# Revit family: Hager-IC-IP40-Transparent_Door-syst-NoHosted-PL-pl
name_source: partatom
category: Electrical Equipment
units: mm (PartAtom-declared; Revit-internal decimal feet)

## family parameters
Always vertical = Yes
Cut with Voids When Loaded = No
Panel Configuration = Two Columns, Circuits Across
Part Type = Panelboard
Room Calculation Point = No
Round Connector Dimension = Use Diameter
Shared = No
Work Plane-Based = Yes

## types (2) — shared parameters
Default Elevation = 1219 mm
EF000007 - Kolor = EV000202 - Biały
EF000116 - Numer RAL = 9010
EF000118 - Z płytą montażową = No
EF000266 - Liczba rzędów = 2
EF000339 - Rodzaj pokrywy = EV004216 - Drzwi
EF001062 - Wykonane zgodnie z Dyrektywą Kompatybilności Elektromagnetycznej EMC = No
EF001088 - Możliwość rozbudowy = Yes
EF001131 - Głębokość wewnętrzna = 72 mm  [stored 0.23622 ft]
EF001134 - Szyna DIN = Yes
EF001596 - Materiał obudowy = EV000139 - Tworzywo sztuczne
EF002950 - Szerokość wyrażona liczbą modułów = 12
EF004462 - Rodzaj zamknięcia = EV000154 - Inne
EF005474 - Stopień ochrony (IP) = EV006415 - IP40
EF006244 - Transparentna pokrywa/drzwi = Yes
EF006306 - Z zamkiem = No
EF009212 - Wykonanie pokrywy = EV000116 - Zamknięty
EF015776 - Listwa zaciskowa uziemienia = Yes
EF015777 - Listwa zaciskowa przewodu neutralnego = Yes
EF015941 - Drzwi przepuszczające sygnał = Yes
HG000001 - Liczba kolumn = 1
HG000002 - Z drzwiami lub pokrywą = Yes
HG000003 - Zakres = IC
HG000005 - Grubość = 3 mm  [stored 0.00984252 ft]
HG000009 - Drzwi dwuskrzydłowe = No
HG000010 - Drzwi asymetryczne = No
HG000011 - Puste rzędy od dołu = No
HG000017 - Odległość między biegunami = 18 mm  [stored 0.0590551 ft]
Manufacturer = Hager
Type Comments = IC
zero-valued in all types: HG000007 - Liczba pustych kolumn, HG000008 - Liczba pustych rzędów

## per-type parameters (varying)
| type | EF000003 - Sposób montażu | EF000008 - Szerokość | EF000040 - Wysokość | EF000049 - Głębokość | EF000218 - Głębokość wbudowania | EF000332 - Wysokość wbudowania | EF000846 - Szerokość wbudowania | HG000004 - Referencja producenta | HG000006 - Montaż podtynkowy | Model |
| Montaż natynkowy IP40 S294 W326.5 G92.5 12 Jednostki dywizyjne - VD212TP | EV000384 - Montaż natynkowy | 294 mm | 326 mm | 92 mm | 0 mm  [stored 0 ft] | 0 mm  [stored 0 ft] | 0 mm  [stored 0 ft] | VD212TP | No | VD212TP |
| Montaż podtynkowy IP40 S308 W351 G93 12 Jednostki dywizyjne - VR212TP | EV000383 - Montaż podtynkowy | 308 mm  [stored 1.0105 ft] | 351 mm  [stored 1.15157 ft] | 93 mm  [stored 0.305118 ft] | 72 mm  [stored 0.23622 ft] | 333 mm  [stored 1.09252 ft] | 290 mm  [stored 0.951444 ft] | VR212TP | Yes | VR212TP |

note: [stored X ft] marks values corroborated as IEEE doubles in the binary element streams (Revit-internal decimal feet)

## geometry (parser evidence)
native form markers: Sweep x13
no freeform markers — native parametric forms only
